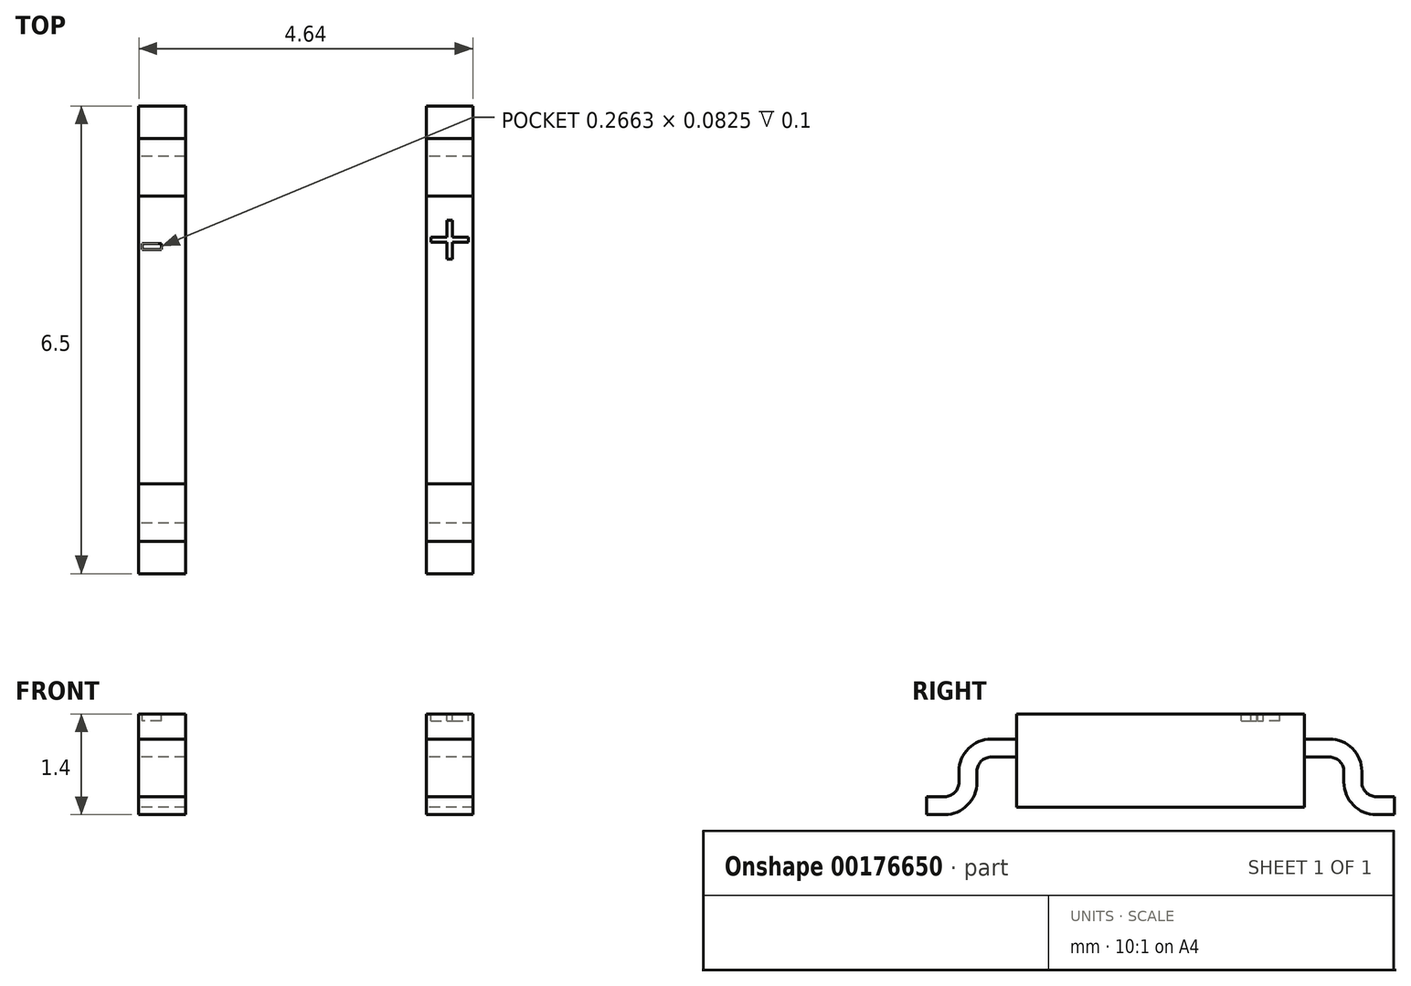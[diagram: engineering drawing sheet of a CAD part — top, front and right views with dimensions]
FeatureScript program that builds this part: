
annotation { "Feature Type Name" : "Feature", "Feature Type Description" : "" }
export const myFeature = defineFeature(function(context is Context, id is Id, definition is map)
    precondition{}
    {
        {
            var Q0;
            Q0=qCreatedBy(makeId("Top.planeOp"),FACE);
            var sketch = newSketch(context, id + "F0", { "sketchPlane" : qUnion([Q0])});
            skLineSegment(sketch, "E0.bottom", {"start": v(2.5, -2) * mm, "end": v(-2.5, -2) * mm});
            skLineSegment(sketch, "E0.top", {"start": v(2.5, 2) * mm, "end": v(-2.5, 2) * mm});
            skLineSegment(sketch, "E0.left", {"start": v(2.5, -2) * mm, "end": v(2.5, 2) * mm});
            skLineSegment(sketch, "E0.right", {"start": v(-2.5, -2) * mm, "end": v(-2.5, 2) * mm});
            skPoint(sketch, "E0.middle", {"position": v(0, 0) * mm});
            skSolve(sketch);
        }
        {
            var Q0;
            Q0=makeQuery(id+"F0.imprint","IMPRINT",FACE,{"disambiguationData":[TD([[makeQuery(id+"F0.imprint","IMPRINT",EDGE,{"derivedFrom":sQuery(id+"F0.wireOp",EDGE,"E0.bottom")}),-1.0]])]});
            extrude(context, id + "F1", {"entities" : qUnion([Q0]), "depth" : 1.3 * mm});
        }
        {
            var Q0;
            Q0=qCreatedBy(makeId("Right.planeOp"),FACE);
            var sketch = newSketch(context, id + "F2", { "sketchPlane" : qUnion([Q0])});
            skLineSegment(sketch, "E1", {"start": v(-3.25, -0.1) * mm, "end": v(-2.55, -0.1) * mm});
            skLineSegment(sketch, "E2", {"start": v(-2.55, -0.1) * mm, "end": v(-2.55, 0.7) * mm});
            skLineSegment(sketch, "E3", {"start": v(-2.55, 0.7) * mm, "end": v(-2, 0.7) * mm});
            skLineSegment(sketch, "E4", {"start": v(-3.25, -0.1) * mm, "end": v(-3.25, 0.15) * mm});
            skLineSegment(sketch, "E5", {"start": v(-2.8, 0.15) * mm, "end": v(-2.8, 0.95) * mm});
            skLineSegment(sketch, "E6", {"start": v(-2.8, 0.95) * mm, "end": v(-2, 0.95) * mm});
            skLineSegment(sketch, "E7", {"start": v(-2, 0.95) * mm, "end": v(-2, 0.7) * mm});
            skLineSegment(sketch, "E8", {"start": v(-2.55, 0.7) * mm, "end": v(-2.8, 0.7) * mm, "construction": true});
            skLineSegment(sketch, "E9", {"start": v(-2.55, 0.7) * mm, "end": v(-2.55, 0.95) * mm, "construction": true});
            skLineSegment(sketch, "E10", {"start": v(0, 0) * mm, "end": v(0, 1.3) * mm, "construction": true});
            skLineSegment(sketch, "E11.MirrorCS", {"start": v(2, 0.95) * mm, "end": v(2, 0.7) * mm});
            skLineSegment(sketch, "E12.MirrorCS", {"start": v(3.25, -0.1) * mm, "end": v(3.25, 0.15) * mm});
            skLineSegment(sketch, "E13.MirrorCS", {"start": v(2.55, 0.7) * mm, "end": v(2.55, 0.95) * mm, "construction": true});
            skLineSegment(sketch, "E14.MirrorCS", {"start": v(2.55, 0.7) * mm, "end": v(2.8, 0.7) * mm, "construction": true});
            skLineSegment(sketch, "E15.MirrorCS", {"start": v(2.8, 0.95) * mm, "end": v(2, 0.95) * mm});
            skLineSegment(sketch, "E16.MirrorCS", {"start": v(2.55, -0.1) * mm, "end": v(2.55, 0.7) * mm});
            skLineSegment(sketch, "E17.MirrorCS", {"start": v(3.25, 0.15) * mm, "end": v(2.8, 0.15) * mm});
            skLineSegment(sketch, "E18.MirrorCS", {"start": v(2.55, 0.7) * mm, "end": v(2, 0.7) * mm});
            skLineSegment(sketch, "E19.MirrorCS", {"start": v(2.8, 0.15) * mm, "end": v(2.8, 0.95) * mm});
            skLineSegment(sketch, "E20.MirrorCS", {"start": v(3.25, -0.1) * mm, "end": v(2.55, -0.1) * mm});
            skLineSegment(sketch, "E21", {"start": v(-2.8, 0.15) * mm, "end": v(-3.25, 0.15) * mm});
            skSolve(sketch);
        }
        {
            var Q0;
            Q0=makeQuery(id+"F2.imprint","IMPRINT",FACE,{"disambiguationData":[TD([[makeQuery(id+"F2.imprint","IMPRINT",EDGE,{"derivedFrom":sQuery(id+"F2.wireOp",EDGE,"E1")}),1.0]])]});
            var Q1;
            Q1=makeQuery(id+"F2.imprint","IMPRINT",FACE,{"disambiguationData":[TD([[makeQuery(id+"F2.imprint","IMPRINT",EDGE,{"derivedFrom":sQuery(id+"F2.wireOp",EDGE,"E11.MirrorCS")}),1.0]])]});
            var Q2;
            Q2=makeQuery(id+"F1.opExtrude","SWEPT_BODY",BODY,{"disambiguationData":[OSD([sQuery(id+"F0.wireOp",EDGE,"E0.bottom"),sQuery(id+"F0.wireOp",EDGE,"E0.top"),sQuery(id+"F0.wireOp",EDGE,"E0.left"),sQuery(id+"F0.wireOp",EDGE,"E0.right")])]});
            extrude(context, id + "F3", {"entities" : qUnion([Q0, Q1]), "endBound" : BoundingType.SYMMETRIC, "endBoundEntityBody" : qUnion([Q2]), "depth" : 5 * mm});
        }
        {
            var Q0;
            Q0=qCreatedBy(makeId("Top.planeOp"),FACE);
            var sketch = newSketch(context, id + "F4", { "sketchPlane" : qUnion([Q0])});
            skLineSegment(sketch, "E22.bottom", {"start": v(1.68, 3.25) * mm, "end": v(-1.68, 3.25) * mm});
            skLineSegment(sketch, "E22.top", {"start": v(1.68, -3.25) * mm, "end": v(-1.68, -3.25) * mm});
            skLineSegment(sketch, "E22.left", {"start": v(1.68, 3.25) * mm, "end": v(1.68, -3.25) * mm});
            skLineSegment(sketch, "E22.right", {"start": v(-1.68, 3.25) * mm, "end": v(-1.68, -3.25) * mm});
            skPoint(sketch, "E22.middle", {"position": v(0, 0) * mm});
            skLineSegment(sketch, "E23.bottom", {"start": v(2.5, -3.25) * mm, "end": v(2.32, -3.25) * mm});
            skLineSegment(sketch, "E23.top", {"start": v(2.5, 3.25) * mm, "end": v(2.32, 3.25) * mm});
            skLineSegment(sketch, "E23.left", {"start": v(2.5, -3.25) * mm, "end": v(2.5, 3.25) * mm});
            skLineSegment(sketch, "E23.right", {"start": v(2.32, -3.25) * mm, "end": v(2.32, 3.25) * mm});
            skLineSegment(sketch, "E24", {"start": v(0, -3.25) * mm, "end": v(0, 3.25) * mm, "construction": true});
            skLineSegment(sketch, "E25.MirrorCS", {"start": v(-2.5, -3.25) * mm, "end": v(-2.5, 3.25) * mm});
            skLineSegment(sketch, "E26.MirrorCS", {"start": v(-2.5, 3.25) * mm, "end": v(-2.33, 3.25) * mm});
            skLineSegment(sketch, "E27.MirrorCS", {"start": v(-2.5, -3.25) * mm, "end": v(-2.32, -3.25) * mm});
            skLineSegment(sketch, "E28.MirrorCS", {"start": v(-2.32, -3.25) * mm, "end": v(-2.32, 3.25) * mm});
            skLineSegment(sketch, "E29", {"start": v(2.32, 0) * mm, "end": v(1.68, 0) * mm, "construction": true});
            skLineSegment(sketch, "E30", {"start": v(-1.68, 0) * mm, "end": v(-2.32, 0) * mm, "construction": true});
            skLineSegment(sketch, "E31", {"start": v(-2, 0) * mm, "end": v(-2, 3.25) * mm, "construction": true});
            skLineSegment(sketch, "E32", {"start": v(2, 0) * mm, "end": v(2, 3.25) * mm, "construction": true});
            skSolve(sketch);
        }
        {
            var Q0;
            Q0 = qSketchRegion(id + "F4", true);
            extrude(context, id + "F5", {"entities" : qUnion([Q0]), "operationType" : NewBodyOperationType.REMOVE, "endBound" : BoundingType.THROUGH_ALL, "depth" : 25 * mm, "hasSecondDirection" : true, "secondDirectionBound" : SecondDirectionBoundingType.THROUGH_ALL, "secondDirectionOppositeDirection" : true, "secondDirectionDepth" : 25 * mm});
        }
        {
            var Q0;
            Q0=makeQuery(id+"F1.opExtrude","CAP_FACE",FACE,{"disambiguationData":[OSD([sQuery(id+"F0.wireOp",EDGE,"E0.bottom"),sQuery(id+"F0.wireOp",EDGE,"E0.top"),sQuery(id+"F0.wireOp",EDGE,"E0.left"),sQuery(id+"F0.wireOp",EDGE,"E0.right")])],"isStart":false});
            var sketch = newSketch(context, id + "F6", { "sketchPlane" : qUnion([Q0])});
            skCircle(sketch, "E33", {"center": v(0, 2) * mm, "radius": 0.62 * mm});
            skText(sketch, "E34", { "text": "+", "fontName": "OpenSans-Regular.ttf"});
            skText(sketch, "E35", { "text": "-", "fontName": "OpenSans-Regular.ttf"});
            const initialGuessF6  = {"E34": [0.00168, 0.001, 1, 0, 0.0008], "E35": [-0.00232, 0.001, 1, 0, 0.0008]};
            skSetInitialGuess(sketch, initialGuessF6);
            skSolve(sketch);
        }
        {
            var Q0;
            Q0 = qSketchRegion(id + "F6", true);
            extrude(context, id + "F7", {"entities" : qUnion([Q0]), "operationType" : NewBodyOperationType.REMOVE, "oppositeDirection" : true, "depth" : 0.1 * mm});
        }
        {
            var Q0;
            {var subQ0=sQuery(id+"F2.wireOp",EDGE,"E17.MirrorCS");var subQ1=sQuery(id+"F2.wireOp",EDGE,"E19.MirrorCS");Q0=makeQuery(id+"F5.boolean.opBoolean","SPLIT",EDGE,{"disambiguationData":[TD([makeQuery(id+"F5.opExtrude","SWEPT_FACE",FACE,{"disambiguationData":[OSD([sQuery(id+"F4.wireOp",EDGE,"E22.right")])]})])],"derivedFrom":makeQuery(id+"F3.opExtrude","SWEPT_EDGE",EDGE,{"disambiguationData":[OSD([subQ0,subQ1])]})});}
            var Q1;
            {var subQ0=sQuery(id+"F2.wireOp",EDGE,"E17.MirrorCS");var subQ1=sQuery(id+"F2.wireOp",EDGE,"E19.MirrorCS");Q1=makeQuery(id+"F5.boolean.opBoolean","SPLIT",EDGE,{"disambiguationData":[TD([makeQuery(id+"F5.opExtrude","SWEPT_FACE",FACE,{"disambiguationData":[OSD([sQuery(id+"F4.wireOp",EDGE,"E22.left")])]})])],"derivedFrom":makeQuery(id+"F3.opExtrude","SWEPT_EDGE",EDGE,{"disambiguationData":[OSD([subQ0,subQ1])]})});}
            var Q2;
            {var subQ0=sQuery(id+"F2.wireOp",EDGE,"E5");var subQ1=sQuery(id+"F2.wireOp",EDGE,"E21");Q2=makeQuery(id+"F5.boolean.opBoolean","SPLIT",EDGE,{"disambiguationData":[TD([makeQuery(id+"F5.opExtrude","SWEPT_FACE",FACE,{"disambiguationData":[OSD([sQuery(id+"F4.wireOp",EDGE,"E22.left")])]})])],"derivedFrom":makeQuery(id+"F3.opExtrude","SWEPT_EDGE",EDGE,{"disambiguationData":[OSD([subQ0,subQ1])]})});}
            var Q3;
            {var subQ0=sQuery(id+"F2.wireOp",EDGE,"E5");var subQ1=sQuery(id+"F2.wireOp",EDGE,"E21");Q3=makeQuery(id+"F5.boolean.opBoolean","SPLIT",EDGE,{"disambiguationData":[TD([makeQuery(id+"F5.opExtrude","SWEPT_FACE",FACE,{"disambiguationData":[OSD([sQuery(id+"F4.wireOp",EDGE,"E22.right")])]})])],"derivedFrom":makeQuery(id+"F3.opExtrude","SWEPT_EDGE",EDGE,{"disambiguationData":[OSD([subQ0,subQ1])]})});}
            var Q4;
            {var subQ0=sQuery(id+"F2.wireOp",EDGE,"E2");var subQ1=sQuery(id+"F2.wireOp",EDGE,"E3");Q4=makeQuery(id+"F5.boolean.opBoolean","SPLIT",EDGE,{"disambiguationData":[TD([makeQuery(id+"F5.opExtrude","SWEPT_FACE",FACE,{"disambiguationData":[OSD([sQuery(id+"F4.wireOp",EDGE,"E22.right")])]})])],"derivedFrom":makeQuery(id+"F3.opExtrude","SWEPT_EDGE",EDGE,{"disambiguationData":[OSD([subQ0,subQ1])]})});}
            var Q5;
            {var subQ0=sQuery(id+"F2.wireOp",EDGE,"E16.MirrorCS");var subQ1=sQuery(id+"F2.wireOp",EDGE,"E18.MirrorCS");Q5=makeQuery(id+"F5.boolean.opBoolean","SPLIT",EDGE,{"disambiguationData":[TD([makeQuery(id+"F5.opExtrude","SWEPT_FACE",FACE,{"disambiguationData":[OSD([sQuery(id+"F4.wireOp",EDGE,"E22.right")])]})])],"derivedFrom":makeQuery(id+"F3.opExtrude","SWEPT_EDGE",EDGE,{"disambiguationData":[OSD([subQ0,subQ1])]})});}
            var Q6;
            {var subQ0=sQuery(id+"F2.wireOp",EDGE,"E16.MirrorCS");var subQ1=sQuery(id+"F2.wireOp",EDGE,"E18.MirrorCS");Q6=makeQuery(id+"F5.boolean.opBoolean","SPLIT",EDGE,{"disambiguationData":[TD([makeQuery(id+"F5.opExtrude","SWEPT_FACE",FACE,{"disambiguationData":[OSD([sQuery(id+"F4.wireOp",EDGE,"E22.left")])]})])],"derivedFrom":makeQuery(id+"F3.opExtrude","SWEPT_EDGE",EDGE,{"disambiguationData":[OSD([subQ0,subQ1])]})});}
            var Q7;
            {var subQ0=sQuery(id+"F2.wireOp",EDGE,"E2");var subQ1=sQuery(id+"F2.wireOp",EDGE,"E3");Q7=makeQuery(id+"F5.boolean.opBoolean","SPLIT",EDGE,{"disambiguationData":[TD([makeQuery(id+"F5.opExtrude","SWEPT_FACE",FACE,{"disambiguationData":[OSD([sQuery(id+"F4.wireOp",EDGE,"E22.left")])]})])],"derivedFrom":makeQuery(id+"F3.opExtrude","SWEPT_EDGE",EDGE,{"disambiguationData":[OSD([subQ0,subQ1])]})});}
            fillet(context, id + "F8", {"entities" : qUnion([Q0, Q1, Q2, Q3, Q4, Q5, Q6, Q7]), "radius" : 0.2 * mm, "tangentPropagation" : true, "allowEdgeOverflow" : false});
        }
        {
            var Q0;
            {var subQ0=sQuery(id+"F2.wireOp",EDGE,"E15.MirrorCS");var subQ1=sQuery(id+"F2.wireOp",EDGE,"E19.MirrorCS");Q0=makeQuery(id+"F5.boolean.opBoolean","SPLIT",EDGE,{"disambiguationData":[TD([makeQuery(id+"F5.opExtrude","SWEPT_FACE",FACE,{"disambiguationData":[OSD([sQuery(id+"F4.wireOp",EDGE,"E22.left")])]})])],"derivedFrom":makeQuery(id+"F3.opExtrude","SWEPT_EDGE",EDGE,{"disambiguationData":[OSD([subQ0,subQ1])]})});}
            var Q1;
            {var subQ0=sQuery(id+"F2.wireOp",EDGE,"E15.MirrorCS");var subQ1=sQuery(id+"F2.wireOp",EDGE,"E19.MirrorCS");Q1=makeQuery(id+"F5.boolean.opBoolean","SPLIT",EDGE,{"disambiguationData":[TD([makeQuery(id+"F5.opExtrude","SWEPT_FACE",FACE,{"disambiguationData":[OSD([sQuery(id+"F4.wireOp",EDGE,"E22.right")])]})])],"derivedFrom":makeQuery(id+"F3.opExtrude","SWEPT_EDGE",EDGE,{"disambiguationData":[OSD([subQ0,subQ1])]})});}
            var Q2;
            {var subQ0=sQuery(id+"F2.wireOp",EDGE,"E5");var subQ1=sQuery(id+"F2.wireOp",EDGE,"E6");Q2=makeQuery(id+"F5.boolean.opBoolean","SPLIT",EDGE,{"disambiguationData":[TD([makeQuery(id+"F5.opExtrude","SWEPT_FACE",FACE,{"disambiguationData":[OSD([sQuery(id+"F4.wireOp",EDGE,"E22.left")])]})])],"derivedFrom":makeQuery(id+"F3.opExtrude","SWEPT_EDGE",EDGE,{"disambiguationData":[OSD([subQ0,subQ1])]})});}
            var Q3;
            {var subQ0=sQuery(id+"F2.wireOp",EDGE,"E5");var subQ1=sQuery(id+"F2.wireOp",EDGE,"E6");Q3=makeQuery(id+"F5.boolean.opBoolean","SPLIT",EDGE,{"disambiguationData":[TD([makeQuery(id+"F5.opExtrude","SWEPT_FACE",FACE,{"disambiguationData":[OSD([sQuery(id+"F4.wireOp",EDGE,"E22.right")])]})])],"derivedFrom":makeQuery(id+"F3.opExtrude","SWEPT_EDGE",EDGE,{"disambiguationData":[OSD([subQ0,subQ1])]})});}
            var Q4;
            {var subQ0=sQuery(id+"F2.wireOp",EDGE,"E16.MirrorCS");var subQ1=sQuery(id+"F2.wireOp",EDGE,"E20.MirrorCS");Q4=makeQuery(id+"F5.boolean.opBoolean","SPLIT",EDGE,{"disambiguationData":[TD([makeQuery(id+"F5.opExtrude","SWEPT_FACE",FACE,{"disambiguationData":[OSD([sQuery(id+"F4.wireOp",EDGE,"E22.right")])]})])],"derivedFrom":makeQuery(id+"F3.opExtrude","SWEPT_EDGE",EDGE,{"disambiguationData":[OSD([subQ0,subQ1])]})});}
            var Q5;
            {var subQ0=sQuery(id+"F2.wireOp",EDGE,"E16.MirrorCS");var subQ1=sQuery(id+"F2.wireOp",EDGE,"E20.MirrorCS");Q5=makeQuery(id+"F5.boolean.opBoolean","SPLIT",EDGE,{"disambiguationData":[TD([makeQuery(id+"F5.opExtrude","SWEPT_FACE",FACE,{"disambiguationData":[OSD([sQuery(id+"F4.wireOp",EDGE,"E22.left")])]})])],"derivedFrom":makeQuery(id+"F3.opExtrude","SWEPT_EDGE",EDGE,{"disambiguationData":[OSD([subQ0,subQ1])]})});}
            var Q6;
            {var subQ0=sQuery(id+"F2.wireOp",EDGE,"E1");var subQ1=sQuery(id+"F2.wireOp",EDGE,"E2");Q6=makeQuery(id+"F5.boolean.opBoolean","SPLIT",EDGE,{"disambiguationData":[TD([makeQuery(id+"F5.opExtrude","SWEPT_FACE",FACE,{"disambiguationData":[OSD([sQuery(id+"F4.wireOp",EDGE,"E22.right")])]})])],"derivedFrom":makeQuery(id+"F3.opExtrude","SWEPT_EDGE",EDGE,{"disambiguationData":[OSD([subQ0,subQ1])]})});}
            var Q7;
            {var subQ0=sQuery(id+"F2.wireOp",EDGE,"E1");var subQ1=sQuery(id+"F2.wireOp",EDGE,"E2");Q7=makeQuery(id+"F5.boolean.opBoolean","SPLIT",EDGE,{"disambiguationData":[TD([makeQuery(id+"F5.opExtrude","SWEPT_FACE",FACE,{"disambiguationData":[OSD([sQuery(id+"F4.wireOp",EDGE,"E22.left")])]})])],"derivedFrom":makeQuery(id+"F3.opExtrude","SWEPT_EDGE",EDGE,{"disambiguationData":[OSD([subQ0,subQ1])]})});}
            fillet(context, id + "F9", {"entities" : qUnion([Q0, Q1, Q2, Q3, Q4, Q5, Q6, Q7]), "radius" : 0.45 * mm, "tangentPropagation" : true, "allowEdgeOverflow" : false});
        }
    });
